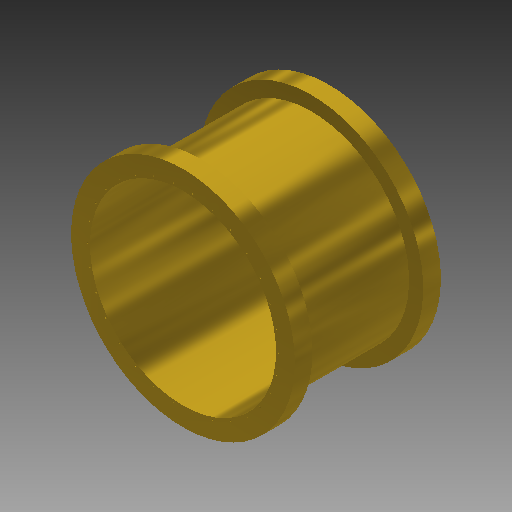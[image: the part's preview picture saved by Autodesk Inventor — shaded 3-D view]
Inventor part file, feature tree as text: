
AUTODESK INVENTOR PART (.ipt)
format: ipt  version: 2017 (Build 210142000, 142)  size: 230,912 bytes
history: native  units: mm (DEFAULTED — no unit token found)
features: sketch x5, extrude x3, revolve x2, pattern_circular x2, projected_geometry x2
ambient origin geometry x8: Origin, YZ Plane, XZ Plane, XY Plane, X Axis, Y Axis, Z Axis, Center Point
bodies: Solid1 (feature_tree)
feature tree (14):
  extrude  "Extrusion1"  Depth=210.7mm
  revolve  "Revolution1"  [1 undecoded]
  pattern_circular  "Circular Pattern1"  Count=30 Angle=360.0deg
  revolve  "Revolution2"  [1 undecoded]
  pattern_circular  "Circular Pattern2"  Angle=90.0deg  [1 undecoded]
  extrude  "Extrusion2"  Depth=18.9992mm TaperAngle=360.0deg
  extrude  "Extrusion3"  Depth=18.9992mm
  sketch  "Sketch1"  dims[d0=200.7mm d1=210.7mm]
  sketch  "Sketch3"  dims[d2=157.48mm d3=0.0mm d15=2.0mm]
  projected_geometry  "Projected Loop1"
  sketch  "Sketch4"  dims[d16=0.5mm]
  projected_geometry  "Projected Loop2"
  sketch  "Sketch5"  dims[d17=90.0deg d18=300.0mm d19=360.0deg]
  sketch  "Sketch6"  dims[d21=2.0mm d22=0.5mm d23=90.0deg d24=300.0mm d25=360.0deg d27=241.3mm d28=18.9992mm d29=0.0mm d30=241.3mm d31=18.9992mm d32=0.0mm]
note: 3 required parameter values undecoded (feature->parameter linkage not recoverable at this tier; creation-order binding heuristic only, values carry confidence <= 0.55)